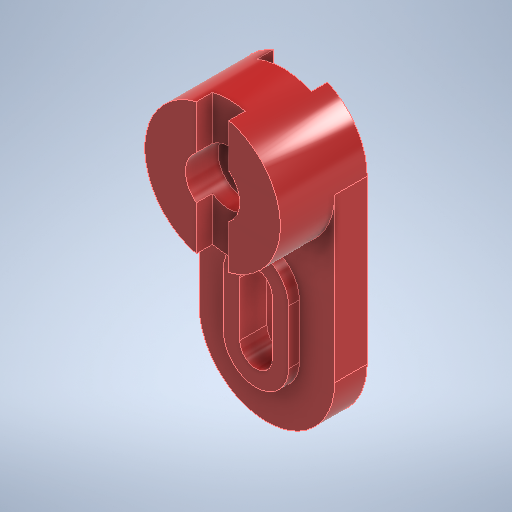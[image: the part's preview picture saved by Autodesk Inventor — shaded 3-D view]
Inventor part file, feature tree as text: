
AUTODESK INVENTOR PART (.ipt)
format: ipt  version: 2025.2 (Build 292293000, 293)  size: 343,040 bytes
history: native  units: in
note: dims shown in document units (in); Inventor stores cm internally (conversion verified against a paired STEP export)
features: extrude x7, sketch x7
ambient origin geometry x8: Origin, YZ Plane, XZ Plane, XY Plane, X Axis, Y Axis, Z Axis, Center Point
bodies: Solid1 (feature_tree)
feature tree (14):
  extrude  "Extrusion1"  Depth=1.9685in
  extrude  "Extrusion2"  Depth=0.4724in TaperAngle=0.0deg
  extrude  "Extrusion3"  Depth=0.7874in TaperAngle=0.0deg
  extrude  "Extrusion4"  Depth=0.4724in
  extrude  "Extrusion5"  Depth=0.2362in TaperAngle=0.0deg
  extrude  "Extrusion6"  Depth=0.2362in TaperAngle=0.0deg
  extrude  "Extrusion7"  Depth=0.2362in
  sketch  "Sketch1"  dims[d0=1.9685in d1=2.3622in]
  sketch  "Sketch2"  dims[d2=0.9843in d3=0.4724in d4=0.0in]
  sketch  "Sketch3"  dims[d5=1.9685in d6=0.7874in d7=0.4724in d8=0.0in d9=0.0in]
  sketch  "Sketch4"  dims[d10=0.7874in d11=0.4724in]
  sketch  "Sketch5"  dims[d12=1.9685in d13=0.2362in d14=0.0in]
  sketch  "Sketch6"  dims[d15=0.7874in d16=0.2362in d17=0.0in]
  sketch  "Sketch7"  dims[d21=0.4724in d22=0.2362in d23=0.1575in d24=0.0in d25=0.7874in d26=0.2362in d27=2.3622in d28=2.3622in d29=0.0in d30=0.0in d31=0.0in d32=0.0in]
